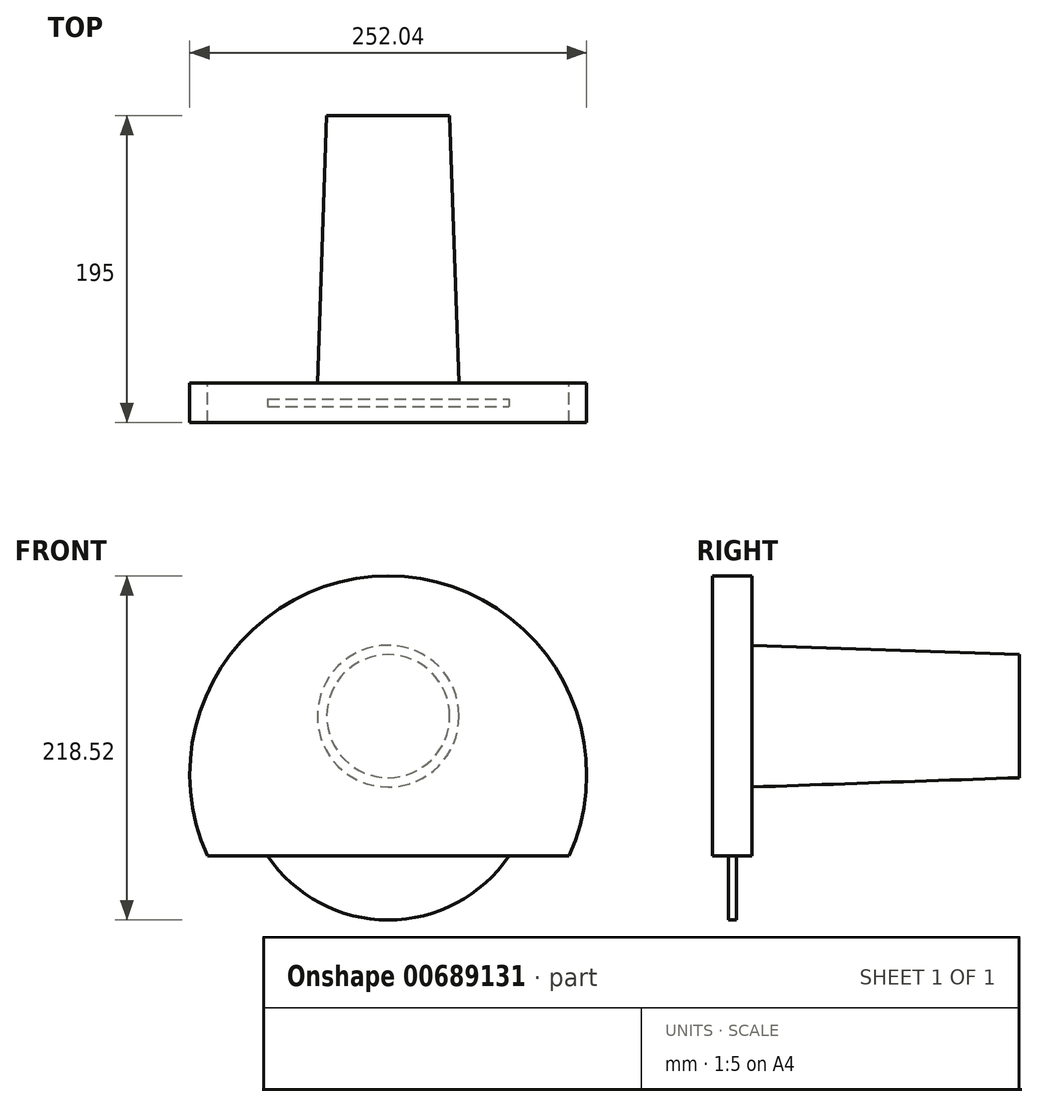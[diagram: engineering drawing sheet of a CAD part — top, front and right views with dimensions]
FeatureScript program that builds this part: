
annotation { "Feature Type Name" : "Feature", "Feature Type Description" : "" }
export const myFeature = defineFeature(function(context is Context, id is Id, definition is map)
    precondition{}
    {
        {
            var Q0;
            Q0=qCreatedBy(makeId("Front.planeOp"),FACE);
            var sketch = newSketch(context, id + "F0", { "sketchPlane" : qUnion([Q0])});
            skCircle(sketch, "E0", {"center": v(0, 0) * mm, "radius": 45 * mm});
            skSolve(sketch);
        }
        {
            var Q0;
            Q0 = qSketchRegion(id + "F0", true);
            extrude(context, id + "F1", {"entities" : qUnion([Q0]), "oppositeDirection" : true, "depth" : 170 * mm, "offsetDistance" : 25 * mm, "hasDraft" : true, "draftAngle" : 2 * degree, "draftPullDirection" : true});
        }
        {
            var Q0;
            Q0=makeQuery(id+"F1.opExtrude","CAP_FACE",FACE,{"disambiguationData":[OSD([sQuery(id+"F0.wireOp",EDGE,"E0")])],"isStart":true});
            var sketch = newSketch(context, id + "F2", { "sketchPlane" : qUnion([Q0])});
            skArc(sketch, "E1", {"start": v(114.87, -88.82) * mm, "mid": v(0, 89.04) * mm, "end": v(-114.87, -88.82) * mm});
            skLineSegment(sketch, "E2", {"start": v(-114.87, -88.82) * mm, "end": v(114.87, -88.82) * mm});
            skSolve(sketch);
        }
        {
            var Q0;
            Q0 = qSketchRegion(id + "F2", true);
            extrude(context, id + "F3", {"entities" : qUnion([Q0]), "operationType" : NewBodyOperationType.ADD, "depth" : 25 * mm, "offsetDistance" : 25 * mm});
        }
        {
            var Q0;
            Q0=makeQuery(id+"F3.opExtrude","CAP_FACE",FACE,{"disambiguationData":[OSD([sQuery(id+"F2.wireOp",EDGE,"E1"),sQuery(id+"F2.wireOp",EDGE,"E2")])],"isStart":false});
            var sketch = newSketch(context, id + "F4", { "sketchPlane" : qUnion([Q0])});
            skCircle(sketch, "E3", {"center": v(0, -36.98) * mm, "radius": 92.5 * mm});
            skSolve(sketch);
        }
        {
            var Q0;
            Q0 = qSketchRegion(id + "F4", true);
            extrude(context, id + "F5", {"entities" : qUnion([Q0]), "operationType" : NewBodyOperationType.ADD, "oppositeDirection" : true, "depth" : 15 * mm, "offsetDistance" : 25 * mm, "hasSecondDirection" : true, "secondDirectionOppositeDirection" : true, "secondDirectionDepth" : 10 * mm});
        }
    });
